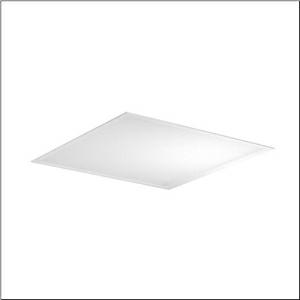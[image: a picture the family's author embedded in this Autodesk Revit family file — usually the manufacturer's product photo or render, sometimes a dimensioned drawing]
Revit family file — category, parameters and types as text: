
# Revit family: apollon_21_square_51mq12wd2114
name_source: partatom
category: Lighting Fixtures
units: mm (PartAtom-declared; Revit-internal decimal feet)

## family parameters
Cut with Voids When Loaded = No
Host = Face
Light Source = No
Part Type = Normal
Room Calculation Point = No
Round Connector Dimension = Use Diameter
Shared = No

## types (1)
- Apollon 21 square (1 x LED, 4100 lm, 24.7 W, 4000K)
    Apparent Load = 25 VA
    CIE Flux Codes = 60 87 97 100 100
    Color Rendering = 90
    Color Temperature = 4000K
    Default Elevation = 1800 mm
    Description = Apollon 21 square, office luminaire, primary optical cover: micro prismatic cover, of PMMA, CAT 2 (L<= 3000cd/m²), light emission: direct distribution, primary light characteristic: symmetric, installation type: lay-in mounting, LED, rated luminous flux: 4.100lm, luminous efficacy: 166lm/W, light colour: 940, colour temperature: 4000K, control gear: DALI 2, Multilumen, with terminal, 5-pole, mains connection: 220..240V, AC/DC, 0/50..60Hz, rated input power: 24.7W, suitable for self-contained emergency lighting element 59MQE002602A with integrated self-test function according to EN 60598-2-22, housing, of aluminium, coated, traffic white (RAL 9016), module: M600, length: 595mm, width: 595mm, height: 55mm, recess depth: 180mm, housing upper side, of sheet steel, galvanised, protection rating (complete): IP20, protection rating (lamp compartment, on room side): IP50, insulation class (complete): insulation class II (safety insulation), certification: CE, ENEC, impact resistance: IK03, permissible operating ambient temperature: -20..+45°C, permissible storage temperature: -40..+80°C, standard: EN 60598-2-22, packaging unit: 1 piece
    Height = 0 mm  [stored 0 ft]
    Lamp = 1 x LED
    Lamp Light Flux = 4100 lm
    Lamp Power = 24.7 W
    Lamp count = 1
    Length = 595 mm
    Luminous efficacy = 166 lm/W
    Manufacturer = Siteco
    ModVariant = No
    Model = 51MQ12WD2114
    Mounting Place = Ceiling
    Mounting Type = Recessed
    Number of Poles = 1
    OnlyDefault = Yes
    Power Factor = 1
    Product Name = Apollon 21 square
    Product group = office luminaire | ceiling recessed
    ProductGroupID = 400
    Protection Class = Protection class II
    Protection Degree = IP 20
    RLX_Detail_Level = 1
    RLX_Emergency_Light_Flux = 0 lm
    RLX_Emergency_Type = 0
    RLX_Emergency_Type_DB = No
    RlxData = <blob elided: 12709 chars, md5=e5d3f052>
    Socket = socket
    Standby Power = 0 W
    System Light Flux = 4100 lm
    System Power = 25 W
    Type Comments = Product without accessories
    Type Image = l_1291049.jpg
    URL = http://relux.com
    VarID = ---
    Voltage = 0 V
    Weight = 0.00 kg
    Width = 595 mm

note: [stored X ft] marks values corroborated as IEEE doubles in the binary element streams (Revit-internal decimal feet)

## geometry (parser evidence)
native form markers: Sweep x10
no freeform markers — native parametric forms only
